# Revit family: York CB-ALE-YK - Linear Active Diffuser,Chilled Beam,Face-Based,Revit 2015 R1.3
name_source: partatom
category: Mechanical Equipment
revit_build: Autodesk Revit 2015 (Build: 20160512_1515(x64)
units: mm (PartAtom-declared; Revit-internal decimal feet)

## types (2) — shared parameters
(0) Front and Back Supply = Yes
(1) Front Supply = No
(2) Back Supply = No
10 Feet = No
10" Oval = No
2 - Two-way Throw = No
2 Feet = Yes
2-Pipe System = Yes
26 White = Yes
2P1C - 2 Pipe, 1 Coil Circuit = Yes
2P2C - 2 Pipe, 2 Coil Circuits = No
3 Feet = No
4 Feet = No
4-Pipe System = No
4P1C - 4 Pipe, 1 Coil Circuit = No
4P2C - 4 Pipe, 2 Coil Circuits = No
5 Feet = No
6 Feet = No
6" Dia. = No
7 Feet = No
8 Feet = No
8" Dia. = No
84- Black Paint = No
9 Feet = No
A = 23 3/4"
A2 = No
A3 = No
A4 = No
Air Inlet Connection Inside Radius = 2"
Air Inlet Connection Radius = 2"
Assembly Code = D3040100
B - One-Way, Back = No
B2 = No
B3 = No
B4 = No
BL - Linear Bar Grillle = No
Bar Top Offset = 1 1/4"
Body Material = Galvanized Steel
Bracket 3 = No
Bracket 4 = No
Bracket Length = 4"
CP - Circular Perforation = Yes
Chilled Water Connection Diameter = 1"
Circular Air Inlet = Yes
Copper Pipe = Copper Pipe
Default Elevation = 0"
Description = Linear Exposed Mounted Active Chilled Beam Supply Diffuser
F - One-Way, Front = Yes
H12 - SS Flex Hose - 12in = No
H18 - SS Flex Hose - 18in = No
H24 - SS FLex Hose - 24in = No
Heating Water Connection Diameter = 1"
Inlet Angle = 180.00°
Inner Oval Inlet Height = 5"
MPT - Male Pipe Thread = No
Manufacturer = York
Max Flow = 0 CFM
Min Flow = 0 CFM
Model = CB-ALE-YK
Nominal Length = 24"
Opening Length = 23 3/4"
Oval Air Inlet = No
Oval Inlet Height = 5 1/4"
Oval Inlet Length = 12 1/2"
Overall Length = 23 3/4"
Pipe Connection Length = 2 1/2"
Pipe Connection Radius = 0"
Pipe Connections Left Hand = No
Pipe Connections Right Hand = Yes
SWT - Sweat = Yes
Second Bracket Distance = 12 1/4"
Select a Beam Length = 1
Select a Finish = 1
Select a Piping Connection Type = 1
Select a Water-Coil Type = 1
Select an Air Nozzle Configuration = 1
Select an Air Throw Pattern = 2
Select the Water-Coil Connection location = 1
Series = Chilled Beam
Side Air Inlet = Yes
Top Air Inlet = No
URL = http://www.york.com
Version = 2
X1 = 22 5/8"
X2 = 22 5/8"
X3 = 22 5/8"
X4 = 22 5/8"
zero-valued in all types: Water Connection Location Selection

## per-type parameters (varying)
- 12" Wide Chill Beam: 12"=Yes; 12" Wide Beam=Yes; 24"=No; 24" Wide Beam=No; 4" Dia.=Yes; 5" Dia.=No; A1=Yes; Air Inlet Front Adapter Visibility=Yes; Angled Housing Notch Height=2 1/2"; B1=No; Back Offset=6"; Bar Array Offset from Center=2 3/16"; Bar Array Quantity=8; Bar Array Spacing=5/8"; Bar Border Offset from Center=2 3/4"; Bar Border Width=1 5/32"; Bar Depth=1 1/4"; Bar Length=22 9/16"; Border Height A=11/16"; Border Height B=1 1/4"; Border Length A=19/32"; Border Length B=1 9/32"; Border Length C=1 9/32"; Bottom Plate Thickness=1"; Circular Plate Lenght=22 9/16"; Circular Plate Width=5 1/2"; Connection Reference Length=1 1/4"; Cooling Water Return Front Offset=9 5/8"; Cooling Water Return Offset=20 5/8"; Cooling Water Supply Front Offset=2 5/8"; Cooling Water Supply Offset=20 5/8"; E=7 1/4"; Front Offset=9 5/8"; Heating Water Return Front Offset=8 5/8"; Heating Water Return Offset=3 3/8"; Heating Water Supply Front Offset=3 5/8"; Heating Water Supply Offset=3 3/8"; Housing Height=9 5/8"; Housing Length=18 3/4"; Housing Notch Height=7 1/8"; Housing Notch Offset=3 5/8"; Housing Width=9 1/2"; Inlet Air Slot Clearance=1/8"; Inlet Depth=4 7/8"; Inlet Length=4 7/8"; Inlet Offset from Top=3 3/8"; Left Void Distance=7 1/8"; Narrow Housing Notch Depth=2 1/2"; Neck Size=4"; Nominal Width=12"; Opening Width=11 3/4"; Overall Height=9 5/8"; Overall Width=14 3/8"; Pipe Connection Back Offset=9 5/8"; Pipe Connection Front Offset=2 5/8"; Pipe Connection Middle Back Offset=8 5/8"; Pipe Connection Middle Front Offset=3 5/8"; Right Void Distance=7 1/8"; Select an Air Inlet Dia.=1; Supply Air Connection Diameter=4"; Supply Inlet Dia=2"; Sweep Void Length=3 1/2"; Total Width=22 7/8"; Wide Housing Notch Length=1/8"; Wide Housing Notch Offset=1/16"; Y1=4 3/4"; Y2=4 3/4"; Y3=2 1/4"; Y4=2 1/4"
- 24" Wide Chilled Beam: 12"=No; 12" Wide Beam=No; 24"=Yes; 24" Wide Beam=Yes; 4" Dia.=No; 5" Dia.=Yes; A1=No; Air Inlet Front Adapter Visibility=No; Angled Housing Notch Height=7 1/8"; B1=Yes; Back Offset=12"; Bar Array Offset from Center=4 3/4"; Bar Array Quantity=20; Bar Array Spacing=1/2"; Bar Border Offset from Center=5 1/4"; Bar Border Width=1 1/2"; Bar Depth=1 3/32"; Bar Length=22 13/32"; Border Height A=5/16"; Border Height B=1 3/32"; Border Length A=11/16"; Border Length B=1 3/4"; Border Length C=2 17/32"; Bottom Plate Thickness=1/4"; Circular Plate Lenght=22 13/32"; Circular Plate Width=10 1/2"; Connection Reference Length=1 5/8"; Cooling Water Return Front Offset=16 1/16"; Cooling Water Return Offset=3 3/4"; Cooling Water Supply Front Offset=7 5/16"; Cooling Water Supply Offset=3 3/4"; E=6 1/4"; Front Offset=13 3/8"; Heating Water Return Front Offset=16 1/16"; Heating Water Return Offset=3 3/4"; Heating Water Supply Front Offset=7 5/16"; Heating Water Supply Offset=3 3/4"; Housing Height=8 3/8"; Housing Length=18 1/2"; Housing Notch Height=3 5/8"; Housing Notch Offset=3 3/4"; Housing Width=20 3/4"; Inlet Air Slot Clearance=1 1/2"; Inlet Depth=3"; Inlet Length=3"; Inlet Offset from Top=3 5/8"; Left Void Distance=8 3/8"; Narrow Housing Notch Depth=1/4"; Neck Size=5"; Nominal Width=24"; Opening Width=23 3/4"; Overall Height=8 3/8"; Overall Width=23 3/4"; Pipe Connection Back Offset=16 1/16"; Pipe Connection Front Offset=7 5/16"; Pipe Connection Middle Back Offset=14 1/16"; Pipe Connection Middle Front Offset=9 5/16"; Right Void Distance=3 5/8"; Select an Air Inlet Dia.=2; Supply Air Connection Diameter=5"; Supply Inlet Dia=2 1/2"; Sweep Void Length=1/8"; Total Width=31 3/8"; Wide Housing Notch Length=2"; Wide Housing Notch Offset=3 3/4"; Y1=15 3/4"; Y2=15 3/4"; Y3=8 1/4"; Y4=8 1/4"

## geometry (parser evidence)
native form markers: Blend x6, Sweep x6
no freeform markers — native parametric forms only
